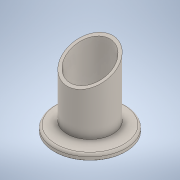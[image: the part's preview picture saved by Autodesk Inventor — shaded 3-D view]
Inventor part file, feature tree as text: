
AUTODESK INVENTOR PART (.ipt)
format: ipt  version: 2021 (Build 250183000, 183)  size: 159,232 bytes
history: native  units: in
note: dims shown in document units (in); Inventor stores cm internally (conversion verified against a paired STEP export)
features: extrude x1, sketch x1, other x1
ambient origin geometry x8: Origin, YZ Plane, XZ Plane, XY Plane, X Axis, Y Axis, Z Axis, Center Point
bodies: Solid1 (feature_tree)
feature tree (3):
  extrude  "Extrusion1"  TaperAngle=0.0deg  [1 undecoded]
  sketch  "Sketch1"  dims[d0=0.1718in d1=0.0in d2=0.0in]
  parser-record x1  (decoder bookkeeping rows leaked as tree rows — omitted from the tree; the rows remain in map.json)
note: 1 required parameter value undecoded (feature->parameter linkage not recoverable at this tier; creation-order binding heuristic only, values carry confidence <= 0.55)
